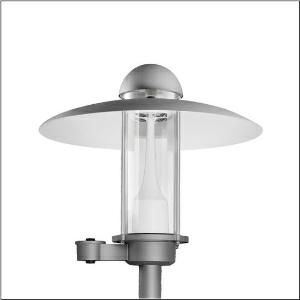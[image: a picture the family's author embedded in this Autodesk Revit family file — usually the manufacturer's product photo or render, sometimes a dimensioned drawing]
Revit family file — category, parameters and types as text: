
# Revit family: city-light_elegance___st1_2a_5xa5263er14h000032_c7d7
name_source: partatom
category: Lighting Fixtures
units: mm (PartAtom-declared; Revit-internal decimal feet)

## family parameters
Cut with Voids When Loaded = No
Host = Face
Light Source = No
Part Type = Normal
Room Calculation Point = No
Round Connector Dimension = Use Diameter
Shared = No

## types (1)
- --- (1 x LED, 1470 lm, 14.2 W, 3000K)
    Apparent Load = 14 VA
    CIE Flux Codes = 22 62 94 98 100
    Color Rendering = 80
    Color Temperature = 3000K
    Default Elevation = 1800 mm
    Description = City-Light Elegance, mast luminaire, Module 540 Plus, primary light control with 3 zone facetted reflector, of plastic, silver coated, highly specular, structured, primary optical cover: cover, of PMMA, transparent, light distribution: ST1.2a, light emission: direct distribution, primary light characteristic: asymmetric, installation type: post-top, LED, High Power LED, rated luminous flux: 1.470lm, luminous efficacy: 104lm/W, light colour: 830, colour temperature: 3000K, control gear: ECG Smart Interface, control: overheat protection, digital communication interface, time-dependent luminous flux control, flexible luminous flux parameterisation, pre-setting: logarithmic dimming characteristic, with terminal, 6-pole, max. 2.5mm², mains connection: 230..240V, AC, 50/60Hz, start of lifetime: 14W, end of service life: 15W, reduction: 8W, luminaire housing, upper part, of aluminium, coated, Siteco® metallic grey (DB 702S), diameter: 750mm, height: 675mm, spigot size: d x l = 76 x 70mm (post-top) | with reducer (optional accessory) 60 x 70mm, post-top mast mounting element, of diecast aluminium, coated, Siteco® metallic grey (DB 702S), Module 540 Plus, traffic white (RAL 9016), Smart Interface below, protection rating (complete): IP65, insulation class (complete): insulation class II (safety insulation), certification: CE, ENEC, VDE, packaging unit: 1 piece

Light Distribution: ST1.2a
    Height = 675 mm
    Lamp = 1 x LED
    Lamp Light Flux = 1470 lm
    Lamp Power = 14.2 W
    Lamp count = 1
    Length = 750 mm
    Luminous efficacy = 104 lm/W
    Manufacturer = Siteco
    ModVariant = No
    Model = 5XA5263ER14H000032
    Number of Poles = 1
    OnlyDefault = Yes
    Power Factor = 1
    Product Name = City-Light Elegance | ST1.2a
    Product group = mast luminaire | pylon top
    ProductGroupID = 6100
    Protection Class = Protection class II
    Protection Degree = IP 65
    RLX_Detail_Level = 1
    RLX_Emergency_Light_Flux = 0 lm
    RLX_Emergency_Type = 0
    RLX_Emergency_Type_DB = No
    RlxData = <blob elided: 72445 chars, md5=82489562>
    Socket = socket
    Standby Power = 0 W
    System Light Flux = 1470 lm
    System Power = 14 W
    Type Comments = factory setting: luminous flux: 100 % | dim-lin: 254 | 516 mA
    Type Image = l_1005991.jpg
    URL = http://relux.com
    VarID = @adj_170623
    Voltage = 0 V
    Weight = 0.00 kg
    Width = 0 mm  [stored 0 ft]

note: [stored X ft] marks values corroborated as IEEE doubles in the binary element streams (Revit-internal decimal feet)

## geometry (parser evidence)
native form markers: Blend x4, Sweep x10
no freeform markers — native parametric forms only
